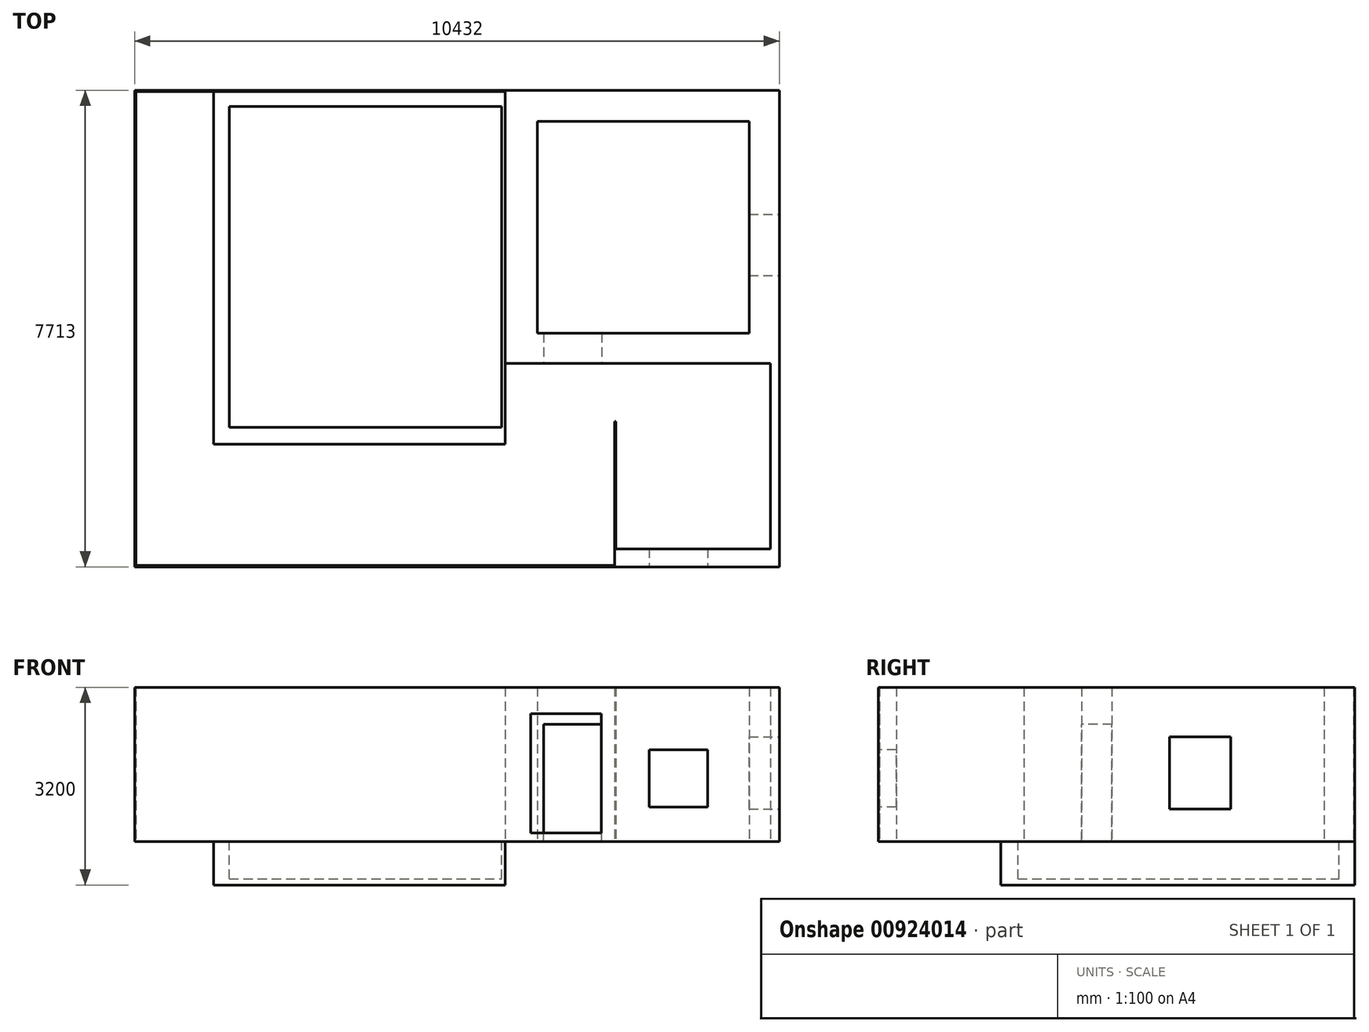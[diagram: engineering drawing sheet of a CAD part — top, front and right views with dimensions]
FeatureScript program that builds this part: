
annotation { "Feature Type Name" : "Feature", "Feature Type Description" : "" }
export const myFeature = defineFeature(function(context is Context, id is Id, definition is map)
    precondition{}
    {
        {
            var Q0;
            Q0=qCreatedBy(makeId("Top.planeOp"),FACE);
            var sketch = newSketch(context, id + "F0", { "sketchPlane" : qUnion([Q0])});
            skLineSegment(sketch, "E0", {"start": v(0, 0) * mm, "end": v(0, 7713) * mm});
            skLineSegment(sketch, "E1", {"start": v(0, 7713) * mm, "end": v(-10432, 7713) * mm});
            skLineSegment(sketch, "E2", {"start": v(-10432, 7713) * mm, "end": v(-10432, 0) * mm});
            skLineSegment(sketch, "E3", {"start": v(-10432, 0) * mm, "end": v(0, 0) * mm});
            skLineSegment(sketch, "E4", {"start": v(0, 3291) * mm, "end": v(-4434, 3291) * mm});
            skLineSegment(sketch, "E5", {"start": v(-4434, 3291) * mm, "end": v(-4434, 7713) * mm});
            skLineSegment(sketch, "E6", {"start": v(-490, 7213) * mm, "end": v(-490, 3781) * mm});
            skLineSegment(sketch, "E7", {"start": v(-490, 3781) * mm, "end": v(-3914, 3781) * mm});
            skLineSegment(sketch, "E8", {"start": v(-3914, 3781) * mm, "end": v(-3914, 7213) * mm});
            skLineSegment(sketch, "E9", {"start": v(-2646.59, 0) * mm, "end": v(-2646.59, 2355.72) * mm});
            skLineSegment(sketch, "E10", {"start": v(-490, 7213) * mm, "end": v(-3914, 7213) * mm});
            skLineSegment(sketch, "E11", {"start": v(-146.59, 291) * mm, "end": v(-2646.59, 291) * mm});
            skLineSegment(sketch, "E12", {"start": v(-146.59, 3291) * mm, "end": v(-146.59, 291) * mm});
            skLineSegment(sketch, "E13.0", {"start": v(-10412, 7693) * mm, "end": v(-10412, 0) * mm});
            skLineSegment(sketch, "E14.0", {"start": v(-4434, 7693) * mm, "end": v(-10412, 7693) * mm});
            skLineSegment(sketch, "E15.0", {"start": v(-10431.58, 20) * mm, "end": v(-2666.59, 20) * mm});
            skLineSegment(sketch, "E16.0", {"start": v(-2666.59, 20) * mm, "end": v(-2666.59, 2355.72) * mm});
            skLineSegment(sketch, "E17", {"start": v(-2646.59, 2355.72) * mm, "end": v(-2666.59, 2355.72) * mm});
            skSolve(sketch);
        }
        {
            var Q0;
            Q0=qCreatedBy(makeId("Top.planeOp"),FACE);
            var sketch = newSketch(context, id + "F1", { "sketchPlane" : qUnion([Q0])});
            skLineSegment(sketch, "E18.bottom", {"start": v(0, 0) * mm, "end": v(-10432, 0) * mm});
            skLineSegment(sketch, "E18.top", {"start": v(0, 7713) * mm, "end": v(-10432, 7713) * mm});
            skLineSegment(sketch, "E18.left", {"start": v(0, 0) * mm, "end": v(0, 7713) * mm});
            skLineSegment(sketch, "E18.right", {"start": v(-10432, 0) * mm, "end": v(-10432, 7713) * mm});
            skLineSegment(sketch, "E19.bottom", {"start": v(-4434, 7713) * mm, "end": v(-9156, 7713) * mm});
            skLineSegment(sketch, "E19.top", {"start": v(-4434, 1984) * mm, "end": v(-9156, 1984) * mm});
            skLineSegment(sketch, "E19.left", {"start": v(-4434, 7713) * mm, "end": v(-4434, 1984) * mm});
            skLineSegment(sketch, "E19.right", {"start": v(-9156, 7713) * mm, "end": v(-9156, 1984) * mm});
            skSolve(sketch);
        }
        {
            var Q0;
            Q0=qCreatedBy(makeId("Top.planeOp"),FACE);
            var sketch = newSketch(context, id + "F2", { "sketchPlane" : qUnion([Q0])});
            skLineSegment(sketch, "E20.bottom", {"start": v(-9156, 1984) * mm, "end": v(-4434, 1984) * mm});
            skLineSegment(sketch, "E20.top", {"start": v(-9156, 7713) * mm, "end": v(-4434, 7713) * mm});
            skLineSegment(sketch, "E20.left", {"start": v(-9156, 1984) * mm, "end": v(-9156, 7713) * mm});
            skLineSegment(sketch, "E20.right", {"start": v(-4434, 1984) * mm, "end": v(-4434, 7713) * mm});
            skLineSegment(sketch, "E21.bottom", {"start": v(-8902.32, 2260.63) * mm, "end": v(-4491.58, 2260.63) * mm});
            skLineSegment(sketch, "E21.top", {"start": v(-8902.32, 7454.2) * mm, "end": v(-4491.58, 7454.2) * mm});
            skLineSegment(sketch, "E21.left", {"start": v(-8902.32, 2260.63) * mm, "end": v(-8902.32, 7454.2) * mm});
            skLineSegment(sketch, "E21.right", {"start": v(-4491.58, 2260.63) * mm, "end": v(-4491.58, 7454.2) * mm});
            skSolve(sketch);
        }
        {
            var Q0;
            Q0=qSketchRegion(id+"F2",true);
            var Q1;
            Q1=makeQuery(id+"F2.imprint","IMPRINT",FACE,{"disambiguationData":[TD([[makeQuery(id+"F2.imprint","IMPRINT",EDGE,{"derivedFrom":sQuery(id+"F2.wireOp",EDGE,"E21.bottom")}),1.0]])]});
            extrude(context, id + "F3", {"entities" : qUnion([Q0, Q1]), "oppositeDirection" : true, "depth" : 700 * mm, "offsetDistance" : 25 * mm, "hasSecondDirection" : true, "secondDirectionOppositeDirection" : true, "secondDirectionDepth" : 600 * mm});
        }
        {
            var Q0;
            Q0=qSketchRegion(id+"F2",true);
            extrude(context, id + "F4", {"entities" : qUnion([Q0]), "operationType" : NewBodyOperationType.ADD, "oppositeDirection" : true, "depth" : 600 * mm, "offsetDistance" : 25 * mm});
        }
        {
            var Q0;
            Q0=qSketchRegion(id+"F0",true);
            extrude(context, id + "F5", {"entities" : qUnion([Q0]), "depth" : 2500 * mm, "offsetDistance" : 25 * mm});
        }
        {
            var Q0;
            Q0=qCreatedBy(makeId("Top.planeOp"),FACE);
            var sketch = newSketch(context, id + "F6", { "sketchPlane" : qUnion([Q0])});
            skLineSegment(sketch, "E22.bottom", {"start": v(-3815.46, 3847.92) * mm, "end": v(-2872.6, 3847.92) * mm});
            skLineSegment(sketch, "E22.top", {"start": v(-3815.46, 3184.97) * mm, "end": v(-2872.6, 3184.97) * mm});
            skLineSegment(sketch, "E22.left", {"start": v(-3815.46, 3847.92) * mm, "end": v(-3815.46, 3184.97) * mm});
            skLineSegment(sketch, "E22.right", {"start": v(-2872.6, 3847.92) * mm, "end": v(-2872.6, 3184.97) * mm});
            skSolve(sketch);
        }
        {
            var Q0;
            Q0=qSketchRegion(id+"F6",true);
            extrude(context, id + "F7", {"entities" : qUnion([Q0]), "operationType" : NewBodyOperationType.REMOVE, "depth" : 1900 * mm, "offsetDistance" : 25 * mm, "hasSecondDirection" : true, "secondDirectionOppositeDirection" : false, "secondDirectionDepth" : 10 * mm});
        }
        {
            var Q0;
            Q0=qCreatedBy(makeId("Top.planeOp"),FACE);
            var sketch = newSketch(context, id + "F8", { "sketchPlane" : qUnion([Q0])});
            skLineSegment(sketch, "E23.bottom", {"start": v(-704.25, 5702.9) * mm, "end": v(253.35, 5702.9) * mm});
            skLineSegment(sketch, "E23.top", {"start": v(-704.25, 4715.84) * mm, "end": v(253.35, 4715.84) * mm});
            skLineSegment(sketch, "E23.left", {"start": v(-704.25, 5702.9) * mm, "end": v(-704.25, 4715.84) * mm});
            skLineSegment(sketch, "E23.right", {"start": v(253.35, 5702.9) * mm, "end": v(253.35, 4715.84) * mm});
            skSolve(sketch);
        }
        {
            var Q0;
            Q0=qSketchRegion(id+"F8",true);
            extrude(context, id + "F9", {"entities" : qUnion([Q0]), "operationType" : NewBodyOperationType.REMOVE, "depth" : 1700 * mm, "offsetDistance" : 25 * mm, "hasSecondDirection" : true, "secondDirectionOppositeDirection" : false, "secondDirectionDepth" : 530 * mm});
        }
        {
            var Q0;
            Q0=qCreatedBy(makeId("Top.planeOp"),FACE);
            var sketch = newSketch(context, id + "F10", { "sketchPlane" : qUnion([Q0])});
            skLineSegment(sketch, "E24.bottom", {"start": v(-2105.62, 419.79) * mm, "end": v(-1163.47, 419.79) * mm});
            skLineSegment(sketch, "E24.top", {"start": v(-2105.62, -203.48) * mm, "end": v(-1163.47, -203.48) * mm});
            skLineSegment(sketch, "E24.left", {"start": v(-2105.62, 419.79) * mm, "end": v(-2105.62, -203.48) * mm});
            skLineSegment(sketch, "E24.right", {"start": v(-1163.47, 419.79) * mm, "end": v(-1163.47, -203.48) * mm});
            skSolve(sketch);
        }
        {
            var Q0;
            Q0=qSketchRegion(id+"F10",true);
            extrude(context, id + "F11", {"entities" : qUnion([Q0]), "operationType" : NewBodyOperationType.REMOVE, "depth" : 1490 * mm, "offsetDistance" : 25 * mm, "hasSecondDirection" : true, "secondDirectionOppositeDirection" : false, "secondDirectionDepth" : 560 * mm});
        }
        {
            var Q0;
            Q0=qCreatedBy(makeId("Top.planeOp"),FACE);
            var sketch = newSketch(context, id + "F12", { "sketchPlane" : qUnion([Q0])});
            skLineSegment(sketch, "E25.bottom", {"start": v(-4022.07, 262.89) * mm, "end": v(-2884.42, 262.89) * mm});
            skLineSegment(sketch, "E25.top", {"start": v(-4022.07, -400.74) * mm, "end": v(-2884.42, -400.74) * mm});
            skLineSegment(sketch, "E25.left", {"start": v(-4022.07, 262.89) * mm, "end": v(-4022.07, -400.74) * mm});
            skLineSegment(sketch, "E25.right", {"start": v(-2884.42, 262.89) * mm, "end": v(-2884.42, -400.74) * mm});
            skSolve(sketch);
        }
        {
            var Q0;
            Q0=qSketchRegion(id+"F12",true);
            extrude(context, id + "F13", {"entities" : qUnion([Q0]), "operationType" : NewBodyOperationType.REMOVE, "depth" : 2070 * mm, "offsetDistance" : 25 * mm, "hasSecondDirection" : true, "secondDirectionOppositeDirection" : false, "secondDirectionDepth" : 140 * mm});
        }
    });
